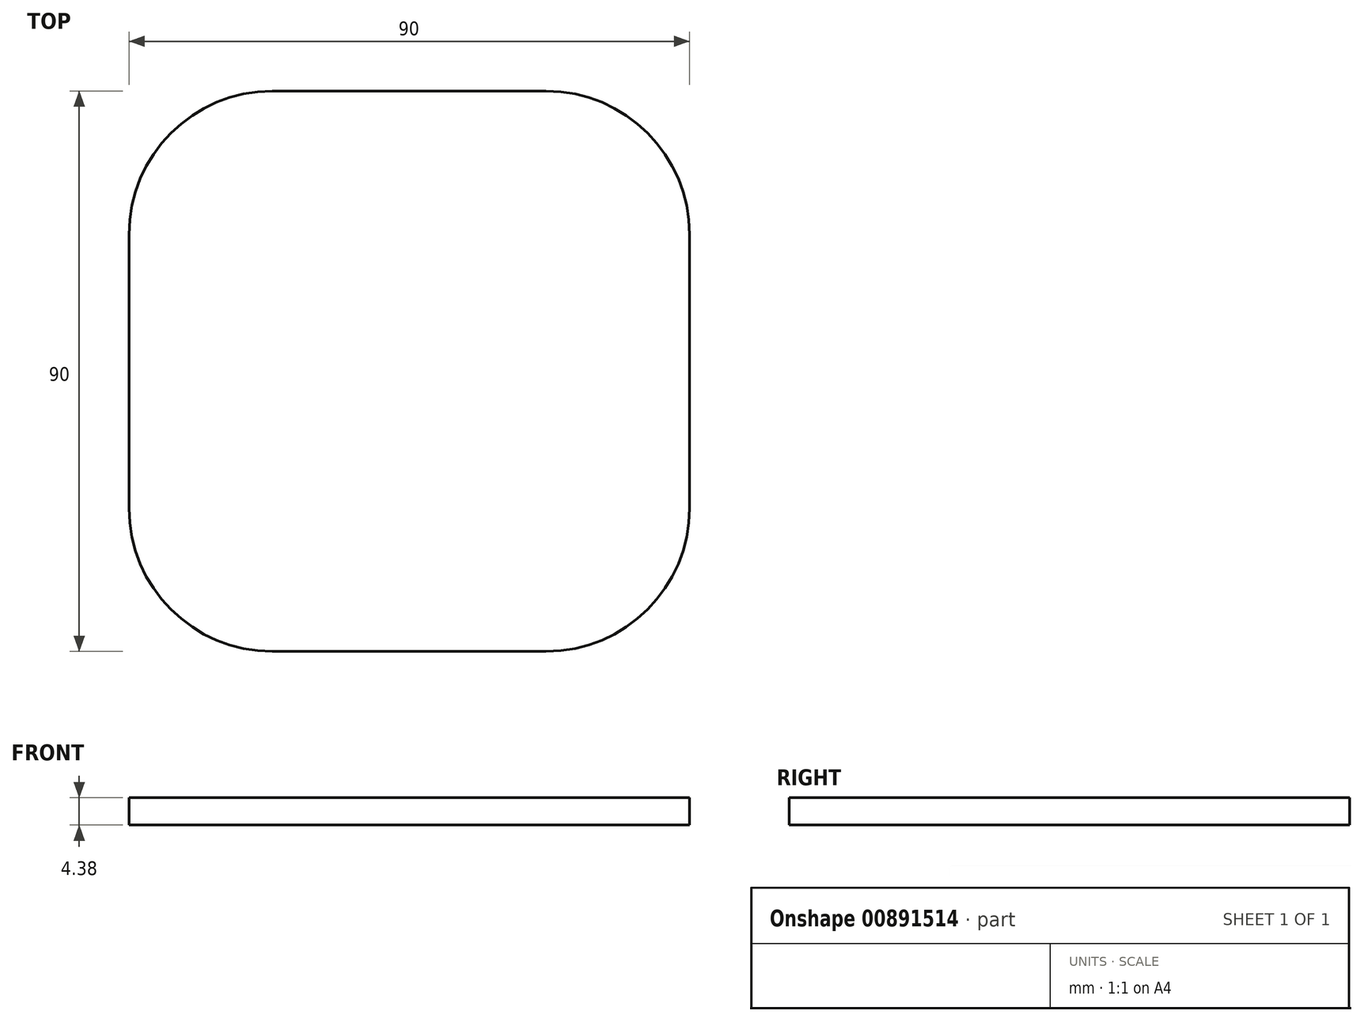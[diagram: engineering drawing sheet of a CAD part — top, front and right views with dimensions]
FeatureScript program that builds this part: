
annotation { "Feature Type Name" : "Feature", "Feature Type Description" : "" }
export const myFeature = defineFeature(function(context is Context, id is Id, definition is map)
    precondition{}
    {
        {
            var Q0;
            Q0=qCreatedBy(makeId("Top.planeOp"),FACE);
            var sketch = newSketch(context, id + "F0", { "sketchPlane" : qUnion([Q0])});
            skLineSegment(sketch, "E0.bottom", {"start": v(45, -45) * mm, "end": v(-45, -45) * mm});
            skLineSegment(sketch, "E0.top", {"start": v(45, 45) * mm, "end": v(-45, 45) * mm});
            skLineSegment(sketch, "E0.left", {"start": v(45, -45) * mm, "end": v(45, 45) * mm});
            skLineSegment(sketch, "E0.right", {"start": v(-45, -45) * mm, "end": v(-45, 45) * mm});
            skPoint(sketch, "E0.middle", {"position": v(0, 0) * mm});
            skSolve(sketch);
        }
        {
            var Q0;
            Q0 = qSketchRegion(id + "F0", true);
            extrude(context, id + "F1", {"entities" : qUnion([Q0]), "depth" : 4.38 * mm, "offsetDistance" : 25.4 * mm});
        }
        {
            var Q0;
            Q0=makeQuery(id+"F1.opExtrude","SWEPT_EDGE",EDGE,{"disambiguationData":[OSD([sQuery(id+"F0.wireOp",EDGE,"E0.top"),sQuery(id+"F0.wireOp",EDGE,"E0.left")])]});
            var Q1;
            Q1=makeQuery(id+"F1.opExtrude","SWEPT_EDGE",EDGE,{"disambiguationData":[OSD([sQuery(id+"F0.wireOp",EDGE,"E0.bottom"),sQuery(id+"F0.wireOp",EDGE,"E0.left")])]});
            var Q2;
            Q2=makeQuery(id+"F1.opExtrude","SWEPT_EDGE",EDGE,{"disambiguationData":[OSD([sQuery(id+"F0.wireOp",EDGE,"E0.bottom"),sQuery(id+"F0.wireOp",EDGE,"E0.right")])]});
            var Q3;
            Q3=makeQuery(id+"F1.opExtrude","SWEPT_EDGE",EDGE,{"disambiguationData":[OSD([sQuery(id+"F0.wireOp",EDGE,"E0.top"),sQuery(id+"F0.wireOp",EDGE,"E0.right")])]});
            fillet(context, id + "F2", {"entities" : qUnion([Q0, Q1, Q2, Q3]), "radius" : 23.02 * mm, "tangentPropagation" : true, "allowEdgeOverflow" : false});
        }
    });
